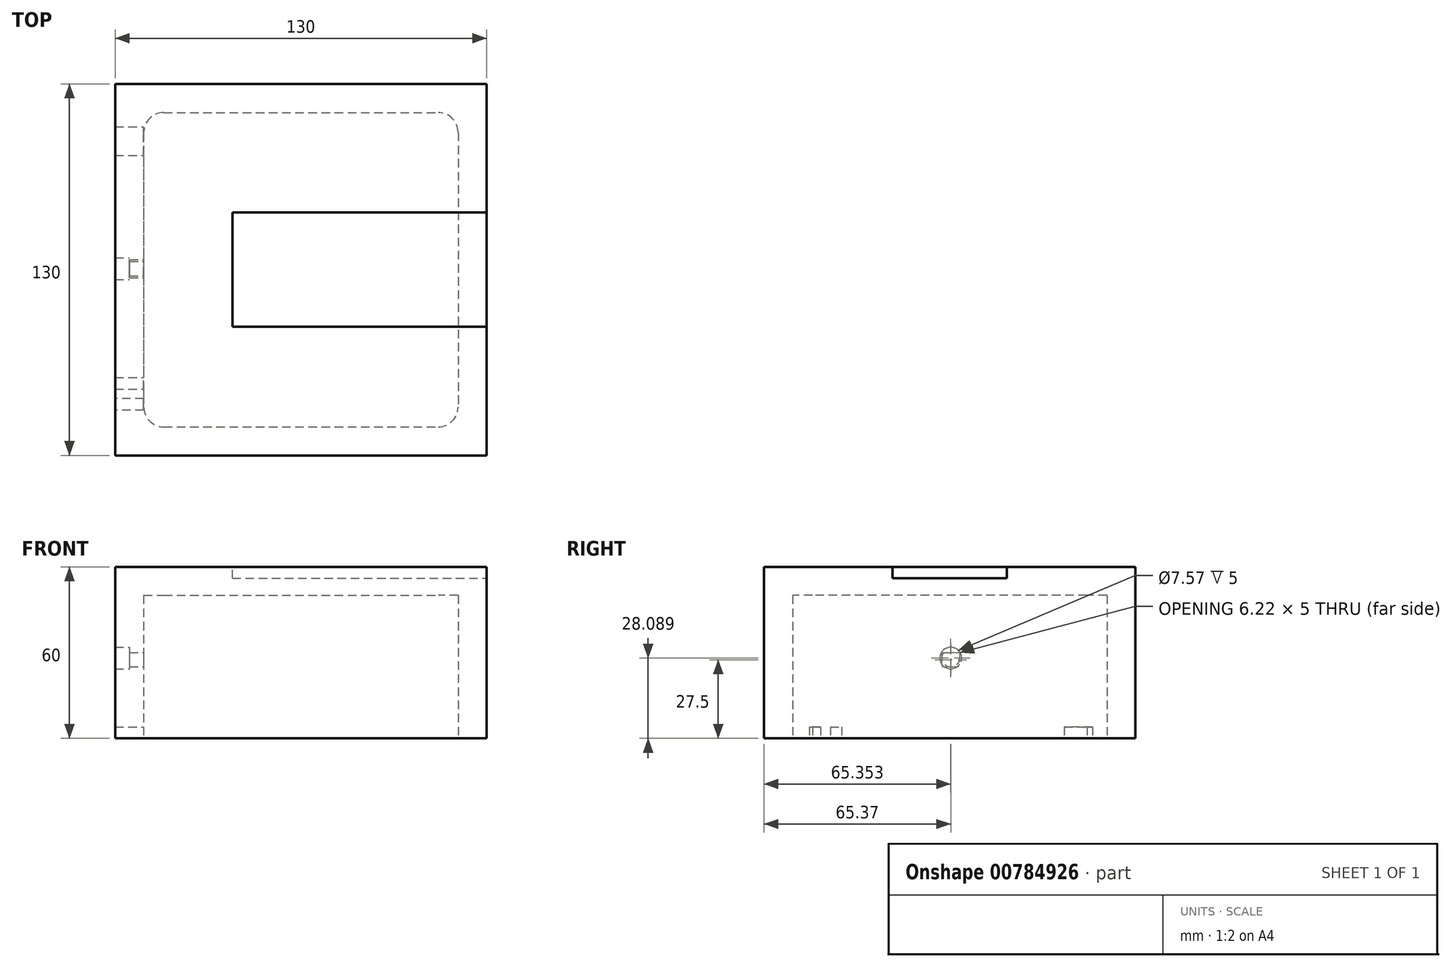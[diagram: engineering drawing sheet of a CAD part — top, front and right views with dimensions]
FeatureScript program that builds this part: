
annotation { "Feature Type Name" : "Feature", "Feature Type Description" : "" }
export const myFeature = defineFeature(function(context is Context, id is Id, definition is map)
    precondition{}
    {
        {
            var Q0;
            Q0=qCreatedBy(makeId("Top.planeOp"),FACE);
            var sketch = newSketch(context, id + "F0", { "sketchPlane" : qUnion([Q0])});
            skLineSegment(sketch, "E0.bottom", {"start": v(-65, 65) * mm, "end": v(65, 65) * mm});
            skLineSegment(sketch, "E0.top", {"start": v(-65, -65) * mm, "end": v(65, -65) * mm});
            skLineSegment(sketch, "E0.left", {"start": v(-65, 65) * mm, "end": v(-65, -65) * mm});
            skLineSegment(sketch, "E0.right", {"start": v(65, 65) * mm, "end": v(65, -65) * mm});
            skPoint(sketch, "E0.middle", {"position": v(0, 0) * mm});
            skSolve(sketch);
        }
        {
            var Q0;
            Q0=qSketchRegion(id+"F0",true);
            extrude(context, id + "F1", {"entities" : qUnion([Q0]), "depth" : 60 * mm, "offsetDistance" : 25 * mm});
        }
        {
            var Q0;
            Q0=qCreatedBy(makeId("Top.planeOp"),FACE);
            var sketch = newSketch(context, id + "F2", { "sketchPlane" : qUnion([Q0])});
            skLineSegment(sketch, "E1.bottom", {"start": v(-55, 55) * mm, "end": v(55, 55) * mm});
            skLineSegment(sketch, "E1.top", {"start": v(-55, -55) * mm, "end": v(55, -55) * mm});
            skLineSegment(sketch, "E1.left", {"start": v(-55, 55) * mm, "end": v(-55, -55) * mm});
            skLineSegment(sketch, "E1.right", {"start": v(55, 55) * mm, "end": v(55, -55) * mm});
            skPoint(sketch, "E1.middle", {"position": v(0, 0) * mm});
            skSolve(sketch);
        }
        {
            var Q0;
            Q0=makeQuery(id+"F2.imprint","IMPRINT",FACE,{"disambiguationData":[TD([[makeQuery(id+"F2.imprint","IMPRINT",EDGE,{"derivedFrom":sQuery(id+"F2.wireOp",EDGE,"E1.bottom")}),-1.0]])]});
            extrude(context, id + "F3", {"entities" : qUnion([Q0]), "operationType" : NewBodyOperationType.REMOVE, "depth" : 50 * mm, "offsetDistance" : 25 * mm});
        }
        {
            var Q0;
            Q0=makeQuery(id+"F1.opExtrude","CAP_FACE",FACE,{"disambiguationData":[OSD([sQuery(id+"F0.wireOp",EDGE,"E0.bottom"),sQuery(id+"F0.wireOp",EDGE,"E0.top"),sQuery(id+"F0.wireOp",EDGE,"E0.left"),sQuery(id+"F0.wireOp",EDGE,"E0.right")])],"isStart":false});
            var sketch = newSketch(context, id + "F4", { "sketchPlane" : qUnion([Q0])});
            skLineSegment(sketch, "E2.bottom", {"start": v(-24, -20) * mm, "end": v(65, -20) * mm});
            skLineSegment(sketch, "E2.top", {"start": v(-24, 20) * mm, "end": v(65, 20) * mm});
            skLineSegment(sketch, "E2.left", {"start": v(-24, -20) * mm, "end": v(-24, 20) * mm});
            skLineSegment(sketch, "E2.right", {"start": v(65, -20) * mm, "end": v(65, 20) * mm});
            skSolve(sketch);
        }
        {
            var Q0;
            Q0=qSketchRegion(id+"F4",true);
            extrude(context, id + "F5", {"entities" : qUnion([Q0]), "operationType" : NewBodyOperationType.REMOVE, "oppositeDirection" : true, "depth" : 4 * mm, "offsetDistance" : 25 * mm});
        }
        {
            var Q0;
            Q0=makeQuery(id+"F3.boolean.opBoolean","COPY",EDGE,{"derivedFrom":makeQuery(id+"F3.opExtrude","SWEPT_EDGE",EDGE,{"disambiguationData":[OSD([sQuery(id+"F2.wireOp",EDGE,"E1.top"),sQuery(id+"F2.wireOp",EDGE,"E1.right")])]})});
            var Q1;
            Q1=makeQuery(id+"F3.boolean.opBoolean","COPY",EDGE,{"derivedFrom":makeQuery(id+"F3.opExtrude","SWEPT_EDGE",EDGE,{"disambiguationData":[OSD([sQuery(id+"F2.wireOp",EDGE,"E1.bottom"),sQuery(id+"F2.wireOp",EDGE,"E1.right")])]})});
            var Q2;
            Q2=makeQuery(id+"F3.boolean.opBoolean","COPY",EDGE,{"derivedFrom":makeQuery(id+"F3.opExtrude","SWEPT_EDGE",EDGE,{"disambiguationData":[OSD([sQuery(id+"F2.wireOp",EDGE,"E1.bottom"),sQuery(id+"F2.wireOp",EDGE,"E1.left")])]})});
            var Q3;
            Q3=makeQuery(id+"F3.boolean.opBoolean","COPY",EDGE,{"derivedFrom":makeQuery(id+"F3.opExtrude","SWEPT_EDGE",EDGE,{"disambiguationData":[OSD([sQuery(id+"F2.wireOp",EDGE,"E1.top"),sQuery(id+"F2.wireOp",EDGE,"E1.left")])]})});
            fillet(context, id + "F6", {"entities" : qUnion([Q0, Q1, Q2, Q3]), "radius" : 7 * mm, "tangentPropagation" : true, "allowEdgeOverflow" : false});
        }
        {
            var Q0;
            Q0=makeQuery(id+"F0.imprint","IMPRINT",FACE,{"disambiguationData":[TD([[makeQuery(id+"F0.imprint","IMPRINT",EDGE,{"derivedFrom":sQuery(id+"F0.wireOp",EDGE,"E0.bottom")}),-1.0]])]});
            var sketch = newSketch(context, id + "F7", { "sketchPlane" : qUnion([Q0])});
            skLineSegment(sketch, "E3.bottom", {"start": v(-65, -41.78) * mm, "end": v(-55, -41.78) * mm});
            skLineSegment(sketch, "E3.top", {"start": v(-65, -37.78) * mm, "end": v(-55, -37.78) * mm});
            skLineSegment(sketch, "E3.left", {"start": v(-65, -41.78) * mm, "end": v(-65, -37.78) * mm});
            skLineSegment(sketch, "E3.right", {"start": v(-55, -41.78) * mm, "end": v(-55, -37.78) * mm});
            skPoint(sketch, "E3.middle", {"position": v(-60, -39.78) * mm});
            skSolve(sketch);
        }
        {
            var Q0;
            Q0=qSketchRegion(id+"F7",true);
            extrude(context, id + "F8", {"entities" : qUnion([Q0]), "operationType" : NewBodyOperationType.REMOVE, "depth" : 4 * mm, "offsetDistance" : 25 * mm});
        }
        {
            var Q0;
            Q0=makeQuery(id+"F0.imprint","IMPRINT",FACE,{"disambiguationData":[TD([[makeQuery(id+"F0.imprint","IMPRINT",EDGE,{"derivedFrom":sQuery(id+"F0.wireOp",EDGE,"E0.bottom")}),-1.0]])]});
            var sketch = newSketch(context, id + "F9", { "sketchPlane" : qUnion([Q0])});
            skLineSegment(sketch, "E4.bottom", {"start": v(-55, -49.14) * mm, "end": v(-65, -49.14) * mm});
            skLineSegment(sketch, "E4.top", {"start": v(-55, -45.14) * mm, "end": v(-65, -45.14) * mm});
            skLineSegment(sketch, "E4.left", {"start": v(-55, -49.14) * mm, "end": v(-55, -45.14) * mm});
            skLineSegment(sketch, "E4.right", {"start": v(-65, -49.14) * mm, "end": v(-65, -45.14) * mm});
            skSolve(sketch);
        }
        {
            var Q0;
            Q0=qSketchRegion(id+"F9",true);
            extrude(context, id + "F10", {"entities" : qUnion([Q0]), "operationType" : NewBodyOperationType.REMOVE, "depth" : 4 * mm, "offsetDistance" : 25 * mm});
        }
        {
            var Q0;
            Q0=makeQuery(id+"F0.imprint","IMPRINT",FACE,{"disambiguationData":[TD([[makeQuery(id+"F0.imprint","IMPRINT",EDGE,{"derivedFrom":sQuery(id+"F0.wireOp",EDGE,"E0.bottom")}),-1.0]])]});
            var sketch = newSketch(context, id + "F11", { "sketchPlane" : qUnion([Q0])});
            skLineSegment(sketch, "E5.bottom", {"start": v(-65, 50) * mm, "end": v(-55, 50) * mm});
            skLineSegment(sketch, "E5.top", {"start": v(-65, 40) * mm, "end": v(-55, 40) * mm});
            skLineSegment(sketch, "E5.left", {"start": v(-65, 40) * mm, "end": v(-65, 50) * mm});
            skLineSegment(sketch, "E5.right", {"start": v(-55, 40) * mm, "end": v(-55, 50) * mm});
            skSolve(sketch);
        }
        {
            var Q0;
            Q0=qSketchRegion(id+"F11",true);
            extrude(context, id + "F12", {"entities" : qUnion([Q0]), "operationType" : NewBodyOperationType.REMOVE, "depth" : 4 * mm, "offsetDistance" : 25 * mm});
        }
        {
            var Q0;
            Q0=makeQuery(id+"F1.opExtrude","SWEPT_FACE",FACE,{"disambiguationData":[OSD([sQuery(id+"F0.wireOp",EDGE,"E0.left")])]});
            cPlane(context, id + "F13", {"entities" : qUnion([Q0]), "cplaneType" : CPlaneType.OFFSET, "offset" : 10 * mm, "oppositeDirection" : true, "width" : 150 * mm, "height" : 150 * mm});
        }
        {
            var Q0;
            Q0=qCreatedBy(id+"F13.planeOp",FACE);
            var sketch = newSketch(context, id + "F14", { "sketchPlane" : qUnion([Q0])});
            skLineSegment(sketch, "E6", {"start": v(2.13, 30) * mm, "end": v(-2.87, 30) * mm});
            skArc(sketch, "E7", {"start": v(-2.87, 30) * mm, "mid": v(-0.37, 25) * mm, "end": v(2.13, 30) * mm});
            skSolve(sketch);
        }
        {
            var Q0;
            Q0=qSketchRegion(id+"F14",true);
            extrude(context, id + "F15", {"entities" : qUnion([Q0]), "operationType" : NewBodyOperationType.REMOVE, "depth" : 5 * mm, "offsetDistance" : 25 * mm});
        }
        {
            var Q0;
            Q0=makeQuery(id+"F1.opExtrude","SWEPT_FACE",FACE,{"disambiguationData":[OSD([sQuery(id+"F0.wireOp",EDGE,"E0.left")])]});
            cPlane(context, id + "F16", {"entities" : qUnion([Q0]), "cplaneType" : CPlaneType.OFFSET, "offset" : 5 * mm, "oppositeDirection" : true, "width" : 150 * mm, "height" : 150 * mm});
        }
        {
            var Q0;
            Q0=qCreatedBy(id+"F16.planeOp",FACE);
            var sketch = newSketch(context, id + "F17", { "sketchPlane" : qUnion([Q0])});
            skCircle(sketch, "E8", {"center": v(-0.35, 28.09) * mm, "radius": 3.78 * mm});
            skPoint(sketch, "E8.first.point", {"position": v(-4.13, 27.87) * mm});
            skPoint(sketch, "E8.second.point", {"position": v(3.43, 27.95) * mm});
            skPoint(sketch, "E8.third.point", {"position": v(0, 31.86) * mm});
            skSolve(sketch);
        }
        {
            var Q0;
            Q0=qSketchRegion(id+"F17",true);
            extrude(context, id + "F18", {"entities" : qUnion([Q0]), "operationType" : NewBodyOperationType.REMOVE, "depth" : 10 * mm, "offsetDistance" : 25 * mm});
        }
    });
